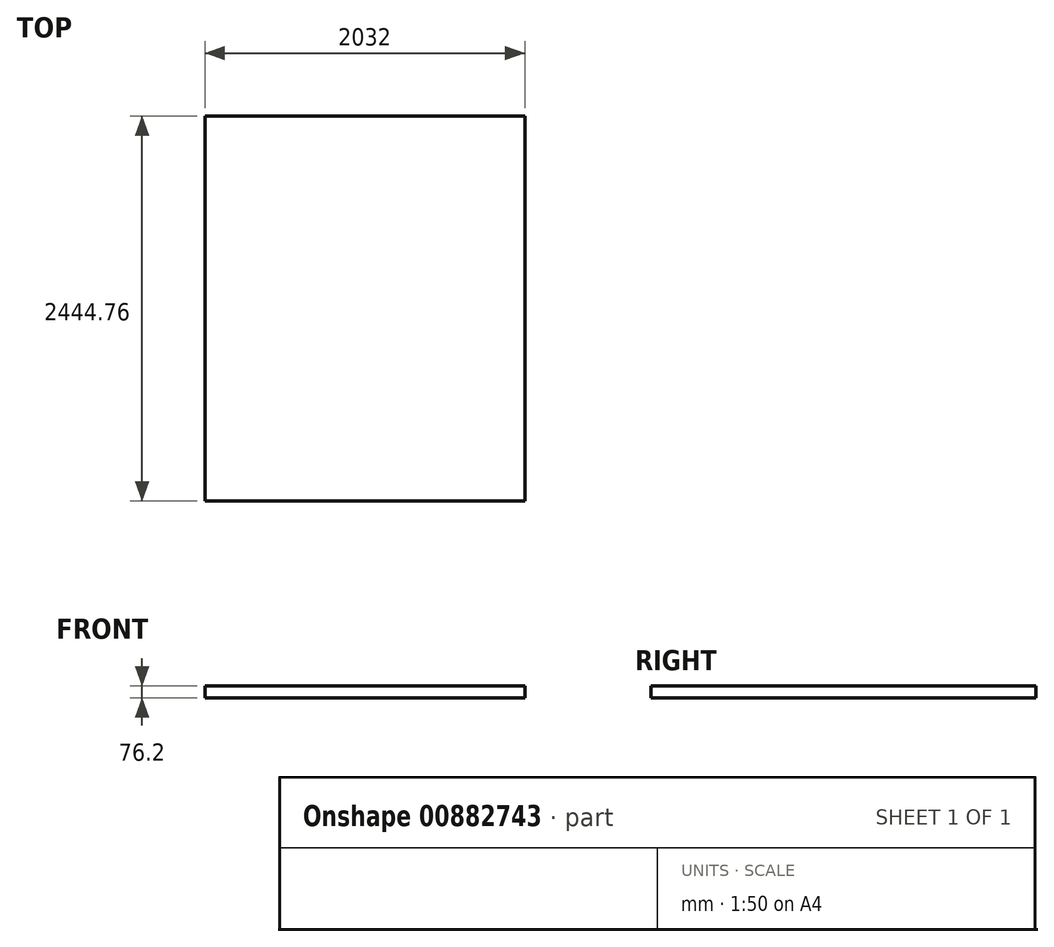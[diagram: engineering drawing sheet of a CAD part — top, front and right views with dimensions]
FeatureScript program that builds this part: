
annotation { "Feature Type Name" : "Feature", "Feature Type Description" : "" }
export const myFeature = defineFeature(function(context is Context, id is Id, definition is map)
    precondition{}
    {
        {
            var Q0;
            Q0=qCreatedBy(makeId("Top.planeOp"),FACE);
            var sketch = newSketch(context, id + "F0", { "sketchPlane" : qUnion([Q0])});
            skLineSegment(sketch, "E0.bottom", {"start": v(615.95, -1222.38) * mm, "end": v(-615.95, -1222.38) * mm});
            skLineSegment(sketch, "E0.top", {"start": v(615.95, 1222.38) * mm, "end": v(-615.95, 1222.38) * mm});
            skLineSegment(sketch, "E0.left", {"start": v(615.95, -1222.38) * mm, "end": v(615.95, 1222.38) * mm});
            skLineSegment(sketch, "E0.right", {"start": v(-615.95, -1222.38) * mm, "end": v(-615.95, 1222.38) * mm});
            skSolve(sketch);
        }
        {
            var Q0;
            Q0 = qSketchRegion(id + "F0", true);
            extrude(context, id + "F1", {"entities" : qUnion([Q0]), "depth" : 76.2 * mm, "offsetDistance" : 25.4 * mm});
        }
        {
            var Q0;
            Q0=makeQuery(id+"F1.opExtrude","SWEPT_FACE",FACE,{"disambiguationData":[OSD([sQuery(id+"F0.wireOp",EDGE,"E0.right")])]});
            extrude(context, id + "F2", {"entities" : qUnion([Q0]), "operationType" : NewBodyOperationType.ADD, "depth" : 400.05 * mm, "offsetDistance" : 25.4 * mm});
        }
        {
            var Q0;
            Q0=makeQuery(id+"F1.opExtrude","SWEPT_FACE",FACE,{"disambiguationData":[OSD([sQuery(id+"F0.wireOp",EDGE,"E0.left")])]});
            extrude(context, id + "F3", {"entities" : qUnion([Q0]), "operationType" : NewBodyOperationType.ADD, "depth" : 400.05 * mm, "offsetDistance" : 25.4 * mm});
        }
    });
